# Revit family: Dosificador de Manos MB-1100
name_source: partatom
category: Plumbing Fixtures
revit_build: Autodesk Revit 2015 (Build: 20140223_1515(x64)
units: mm (PartAtom-declared; Revit-internal decimal feet)

## types (1)
- MB-1100
    Abs Plastic = Plastic
    Air Flow = 0 m³/h
    Aluminum Body = Aluminum
    Anodized Aluminum Finish = Aluminum, Anodized
    Container Capacity = 800 ml
    Current Consumption = 160 A
    Default Elevation = 53 "
    Description = Opera con 4 baterías alcalinas tamaño "AA", Incluye Paquete de Sujeción, Activación Automática por Sensor Infrarrojo
    Detection Range = 3.8 cm -6 cm
    Feeding = 6 Baterias Alcalinas (1.5V) Tipo (AA)
    Feeding Voltage = 5 V
    Manufacturer = HELVEX S.A. DE C.V.
    Model = MB-1100
    Power Consumption = 1 W
    Response Time = 0.5 - 1 mseg
    Total Height = 10.6 "
    Total Length = 4.8 "
    Total Weight = 0.70 kg
    Total Width = 4.2 "
    Type Comments = Dosificador de jabón Líquido Eléctronico de Baterías con Sensor
    Type Image = MB-1100.jpg
    URL = http://www.helvex.com.mx

## geometry (parser evidence)
native form markers: Sweep x6
no freeform markers — native parametric forms only
